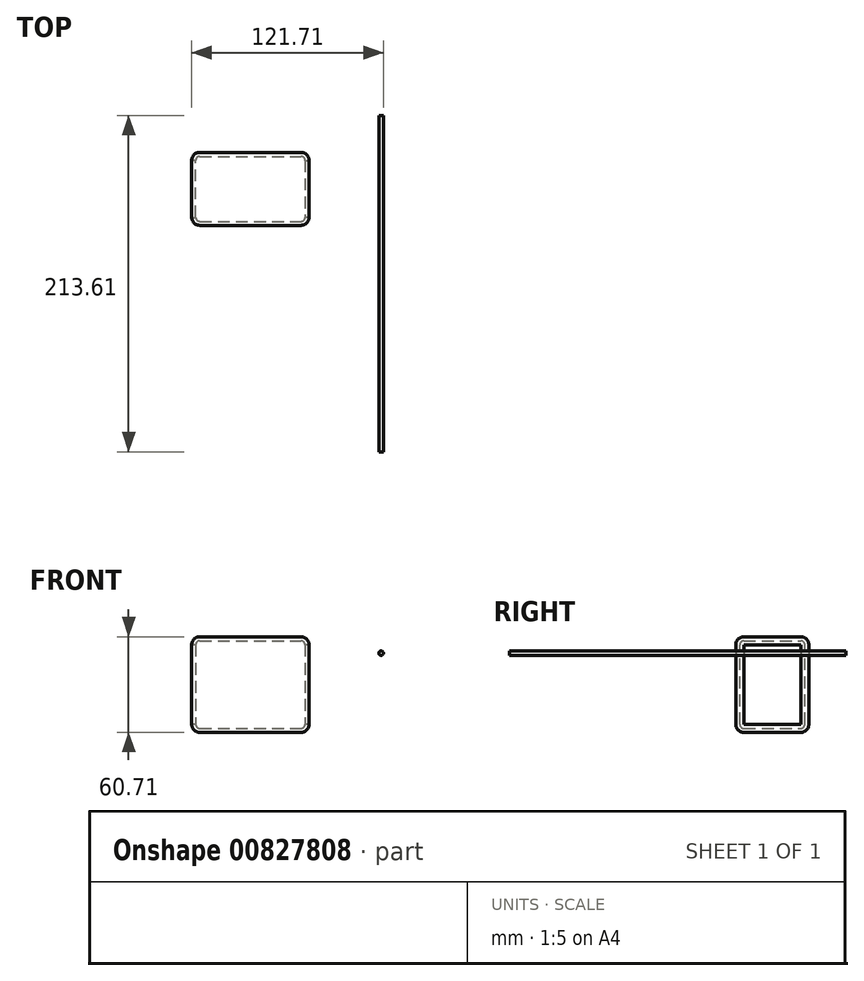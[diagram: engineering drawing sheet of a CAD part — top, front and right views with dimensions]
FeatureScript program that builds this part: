
annotation { "Feature Type Name" : "Feature", "Feature Type Description" : "" }
export const myFeature = defineFeature(function(context is Context, id is Id, definition is map)
    precondition{}
    {
        {
            var Q0;
            Q0=qCreatedBy(makeId("Top.planeOp"),FACE);
            var sketch = newSketch(context, id + "F0", { "sketchPlane" : qUnion([Q0])});
            skLineSegment(sketch, "E0.bottom", {"start": v(-74.46, -23.4) * mm, "end": v(0, -23.4) * mm});
            skLineSegment(sketch, "E0.top", {"start": v(-74.46, -69.76) * mm, "end": v(0, -69.76) * mm});
            skLineSegment(sketch, "E0.left", {"start": v(-74.46, -23.4) * mm, "end": v(-74.46, -69.76) * mm});
            skLineSegment(sketch, "E0.right", {"start": v(0, -23.4) * mm, "end": v(0, -69.76) * mm});
            skSolve(sketch);
        }
        {
            var Q0;
            Q0 = qSketchRegion(id + "F0", true);
            extrude(context, id + "F1", {"entities" : qUnion([Q0]), "depth" : 60.7 * mm, "offsetDistance" : 25.4 * mm});
        }
        {
            var Q0;
            Q0=makeQuery(id+"F1.opExtrude","CAP_FACE",FACE,{"disambiguationData":[OSD([sQuery(id+"F0.wireOp",EDGE,"E0.bottom"),sQuery(id+"F0.wireOp",EDGE,"E0.top"),sQuery(id+"F0.wireOp",EDGE,"E0.left"),sQuery(id+"F0.wireOp",EDGE,"E0.right")])],"isStart":false});
            var Q1;
            Q1=makeQuery(id+"F1.opExtrude","SWEPT_EDGE",EDGE,{"disambiguationData":[OSD([sQuery(id+"F0.wireOp",EDGE,"E0.top"),sQuery(id+"F0.wireOp",EDGE,"E0.right")])]});
            var Q2;
            Q2=makeQuery(id+"F1.opExtrude","SWEPT_FACE",FACE,{"disambiguationData":[OSD([sQuery(id+"F0.wireOp",EDGE,"E0.right")])]});
            var Q3;
            Q3=makeQuery(id+"F1.opExtrude","SWEPT_FACE",FACE,{"disambiguationData":[OSD([sQuery(id+"F0.wireOp",EDGE,"E0.top")])]});
            var Q4;
            Q4=makeQuery(id+"F1.opExtrude","SWEPT_FACE",FACE,{"disambiguationData":[OSD([sQuery(id+"F0.wireOp",EDGE,"E0.left")])]});
            var Q5;
            Q5=makeQuery(id+"F1.opExtrude","CAP_FACE",FACE,{"disambiguationData":[OSD([sQuery(id+"F0.wireOp",EDGE,"E0.bottom"),sQuery(id+"F0.wireOp",EDGE,"E0.top"),sQuery(id+"F0.wireOp",EDGE,"E0.left"),sQuery(id+"F0.wireOp",EDGE,"E0.right")])],"isStart":true});
            fillet(context, id + "F2", {"entities" : qUnion([Q0, Q1, Q2, Q3, Q4, Q5]), "radius" : 5.08 * mm, "tangentPropagation" : true, "allowEdgeOverflow" : false});
        }
        {
            var Q0;
            Q0=makeQuery(id+"F1.opExtrude","SWEPT_FACE",FACE,{"disambiguationData":[OSD([sQuery(id+"F0.wireOp",EDGE,"E0.right")])]});
            var Q1;
            Q1=makeQuery(id+"F1.opExtrude","SWEPT_FACE",FACE,{"disambiguationData":[OSD([sQuery(id+"F0.wireOp",EDGE,"E0.left")])]});
            shell(context, id + "F3", {"entities" : qUnion([Q0, Q1]), "thickness" : 2.54 * mm});
        }
        {
            var Q0;
            Q0=qCreatedBy(makeId("Front.planeOp"),FACE);
            var sketch = newSketch(context, id + "F4", { "sketchPlane" : qUnion([Q0])});
            skCircle(sketch, "E1", {"center": v(45.83, 50.33) * mm, "radius": 1.42 * mm});
            skSolve(sketch);
        }
        {
            var Q0;
            Q0 = qSketchRegion(id + "F4", true);
            extrude(context, id + "F5", {"entities" : qUnion([Q0]), "depth" : 213.61 * mm, "offsetDistance" : 25.4 * mm});
        }
    });
